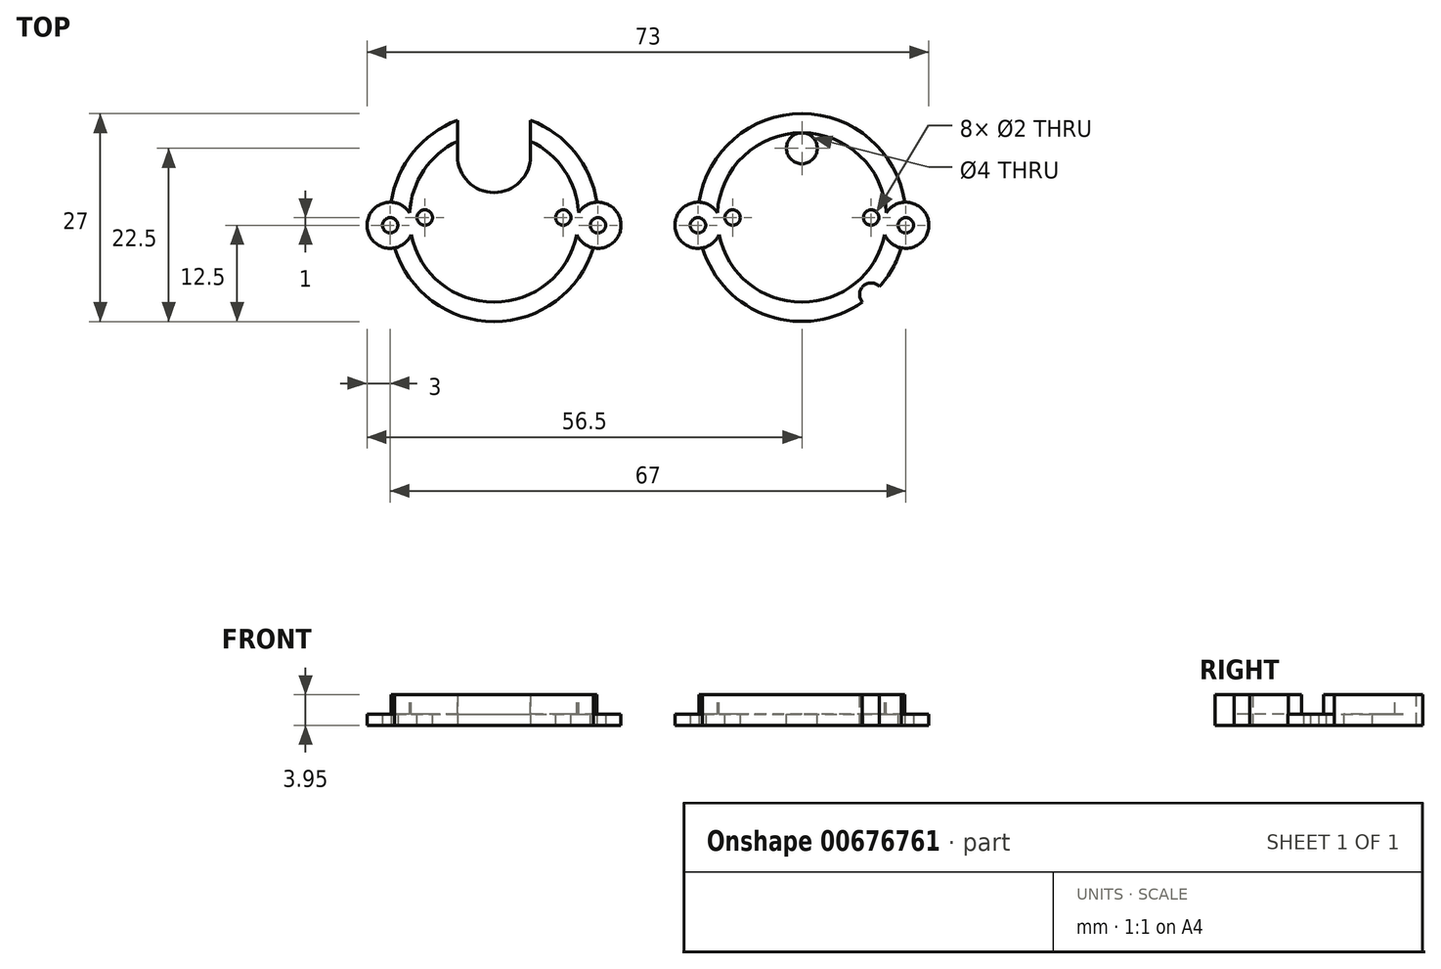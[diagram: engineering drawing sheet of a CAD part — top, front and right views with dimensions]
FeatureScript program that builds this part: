
annotation { "Feature Type Name" : "Feature", "Feature Type Description" : "" }
export const myFeature = defineFeature(function(context is Context, id is Id, definition is map)
    precondition{}
    {
        {
            var Q0;
            Q0=qCreatedBy(makeId("Top.planeOp"),FACE);
            var sketch = newSketch(context, id + "F0", { "sketchPlane" : qUnion([Q0])});
            skArc(sketch, "E0", {"start": v(-12.91, -3.94) * mm, "mid": v(0, -13.5) * mm, "end": v(12.91, -3.94) * mm});
            skCircle(sketch, "E1", {"center": v(-13.5, -1) * mm, "radius": 1 * mm});
            skCircle(sketch, "E2", {"center": v(13.5, -1) * mm, "radius": 1 * mm});
            skArc(sketch, "E3", {"start": v(-12.91, -3.94) * mm, "mid": v(-16.5, -1.22) * mm, "end": v(-13.35, 2) * mm});
            skArc(sketch, "E4", {"start": v(12.91, -3.94) * mm, "mid": v(16.5, -1.22) * mm, "end": v(13.35, 2) * mm});
            skArc(sketch, "E5.trimOffspring", {"start": v(13.35, 2) * mm, "mid": v(0, 13.5) * mm, "end": v(-13.35, 2) * mm});
            skSolve(sketch);
        }
        {
            var Q0;
            Q0=makeQuery(id+"F0.imprint","IMPRINT",FACE,{"disambiguationData":[TD([[makeQuery(id+"F0.imprint","IMPRINT",EDGE,{"derivedFrom":sQuery(id+"F0.wireOp",EDGE,"E0")}),1.0]])]});
            extrude(context, id + "F1", {"entities" : qUnion([Q0]), "depth" : 3.95 * mm, "offsetDistance" : 25 * mm});
        }
        {
            var Q0;
            Q0=makeQuery(id+"F1.opExtrude","CAP_FACE",FACE,{"disambiguationData":[OSD([sQuery(id+"F0.wireOp",EDGE,"E0")])],"isStart":false});
            var sketch = newSketch(context, id + "F2", { "sketchPlane" : qUnion([Q0])});
            skCircle(sketch, "E6", {"center": v(0, 0) * mm, "radius": 11 * mm});
            skSolve(sketch);
        }
        {
            var Q0;
            Q0 = qSketchRegion(id + "F2", true);
            extrude(context, id + "F3", {"entities" : qUnion([Q0]), "operationType" : NewBodyOperationType.REMOVE, "oppositeDirection" : true, "depth" : 2.5 * mm, "offsetDistance" : 25 * mm});
        }
        {
            var Q0;
            Q0=makeQuery(id+"F1.opExtrude","CAP_FACE",FACE,{"disambiguationData":[OSD([sQuery(id+"F0.wireOp",EDGE,"E0"),sQuery(id+"F0.wireOp",EDGE,"E1"),sQuery(id+"F0.wireOp",EDGE,"E2"),sQuery(id+"F0.wireOp",EDGE,"E3"),sQuery(id+"F0.wireOp",EDGE,"E4"),sQuery(id+"F0.wireOp",EDGE,"E5.trimOffspring")])],"isStart":false});
            var sketch = newSketch(context, id + "F4", { "sketchPlane" : qUnion([Q0])});
            skCircle(sketch, "E7", {"center": v(-13.5, -1) * mm, "radius": 3 * mm});
            skCircle(sketch, "E8", {"center": v(13.5, -1) * mm, "radius": 3 * mm});
            skSolve(sketch);
        }
        {
            var Q0;
            Q0 = qSketchRegion(id + "F4", true);
            var Q1;
            Q1=makeQuery(id+"F3.boolean.opBoolean","COPY",FACE,{"derivedFrom":makeQuery(id+"F3.opExtrude","CAP_FACE",FACE,{"disambiguationData":[OSD([sQuery(id+"F2.wireOp",EDGE,"E6")])],"isStart":false})});
            extrude(context, id + "F5", {"entities" : qUnion([Q0]), "operationType" : NewBodyOperationType.REMOVE, "endBound" : BoundingType.UP_TO_SURFACE, "oppositeDirection" : true, "depth" : 25 * mm, "endBoundEntityFace" : qUnion([Q1]), "offsetDistance" : 25 * mm});
        }
        {
            var Q0;
            Q0=makeQuery(id+"F3.boolean.opBoolean","COPY",FACE,{"derivedFrom":makeQuery(id+"F3.opExtrude","CAP_FACE",FACE,{"disambiguationData":[OSD([sQuery(id+"F2.wireOp",EDGE,"E6")])],"isStart":false})});
            var sketch = newSketch(context, id + "F6", { "sketchPlane" : qUnion([Q0])});
            skCircle(sketch, "E9", {"center": v(-9, 0) * mm, "radius": 1 * mm});
            skCircle(sketch, "E10", {"center": v(9, 0) * mm, "radius": 1 * mm});
            skSolve(sketch);
        }
        {
            var Q0;
            Q0=makeQuery(id+"F6.imprint","IMPRINT",FACE,{"disambiguationData":[TD([[makeQuery(id+"F6.imprint","IMPRINT",EDGE,{"derivedFrom":sQuery(id+"F6.wireOp",EDGE,"E9")}),1.0]])]});
            var Q1;
            Q1=makeQuery(id+"F6.imprint","IMPRINT",FACE,{"disambiguationData":[TD([[makeQuery(id+"F6.imprint","IMPRINT",EDGE,{"derivedFrom":sQuery(id+"F6.wireOp",EDGE,"E10")}),1.0]])]});
            extrude(context, id + "F7", {"entities" : qUnion([Q0, Q1]), "operationType" : NewBodyOperationType.REMOVE, "endBound" : BoundingType.THROUGH_ALL, "oppositeDirection" : true, "depth" : 25 * mm, "offsetDistance" : 25 * mm});
        }
        {
            var Q0;
            Q0=makeQuery(id+"F1.opExtrude","SWEPT_BODY",BODY,{"disambiguationData":[OSD([sQuery(id+"F0.wireOp",EDGE,"E0"),sQuery(id+"F0.wireOp",EDGE,"E1"),sQuery(id+"F0.wireOp",EDGE,"E2"),sQuery(id+"F0.wireOp",EDGE,"E3"),sQuery(id+"F0.wireOp",EDGE,"E4"),sQuery(id+"F0.wireOp",EDGE,"E5.trimOffspring")])]});
            transform(context, id + "F8", {"entities" : qUnion([Q0]), "transformType" : TransformType.TRANSLATION_3D, "dx" : 40 * mm, "dy" : 0 * mm, "dz" : 0 * mm, "makeCopy" : true});
        }
        {
            var Q0;
            Q0=makeQuery(id+"F1.opExtrude","CAP_FACE",FACE,{"disambiguationData":[OSD([sQuery(id+"F0.wireOp",EDGE,"E0")])],"isStart":true});
            var sketch = newSketch(context, id + "F9", { "sketchPlane" : qUnion([Q0])});
            skArc(sketch, "E11", {"start": v(4.75, -8) * mm, "mid": v(0, -3.25) * mm, "end": v(-4.75, -8) * mm});
            skLineSegment(sketch, "E12", {"start": v(-4.75, -8) * mm, "end": v(-4.75, -12.64) * mm});
            skLineSegment(sketch, "E13", {"start": v(4.75, -8) * mm, "end": v(4.75, -12.64) * mm});
            skSolve(sketch);
        }
        {
            var Q0;
            Q0=makeQuery(id+"F9.imprint","IMPRINT",FACE,{"disambiguationData":[TD([[makeQuery(id+"F9.imprint","IMPRINT",EDGE,{"derivedFrom":sQuery(id+"F9.wireOp",EDGE,"E11")}),1.0]])]});
            var Q1;
            Q1=makeQuery(id+"F1.opExtrude","CAP_FACE",FACE,{"disambiguationData":[OSD([sQuery(id+"F0.wireOp",EDGE,"E0")])],"isStart":false});
            extrude(context, id + "F10", {"entities" : qUnion([Q0]), "operationType" : NewBodyOperationType.REMOVE, "endBound" : BoundingType.UP_TO_SURFACE, "oppositeDirection" : true, "depth" : 25 * mm, "endBoundEntityFace" : qUnion([Q1]), "offsetDistance" : 25 * mm});
        }
        {
            var Q0;
            {var subQ0=sQuery(id+"F2.wireOp",EDGE,"E6");Q0=makeQuery(id+"F8.opPattern","COPY",FACE,{"derivedFrom":makeQuery(id+"F5.boolean.opBoolean","MERGE",FACE,{"derivedFrom":[makeQuery(id+"F3.boolean.opBoolean","COPY",FACE,{"derivedFrom":makeQuery(id+"F3.opExtrude","CAP_FACE",FACE,{"disambiguationData":[OSD([subQ0])],"isStart":false})}),makeQuery(id+"F5.opExtrude","CAP_FACE",FACE,{"disambiguationData":[OSD([subQ0]),OD(0.0)],"isStart":false}),makeQuery(id+"F5.opExtrude","CAP_FACE",FACE,{"disambiguationData":[OSD([subQ0]),OD(1.0)],"isStart":false})]}),"instanceName":"1"});}
            var sketch = newSketch(context, id + "F11", { "sketchPlane" : qUnion([Q0])});
            skCircle(sketch, "E14", {"center": v(40, 9) * mm, "radius": 2 * mm});
            skCircle(sketch, "E15", {"center": v(49, -10) * mm, "radius": 1.5 * mm});
            skPoint(sketch, "E16", {"position": v(26.5, -1) * mm});
            skSolve(sketch);
        }
        {
            var Q0;
            Q0=makeQuery(id+"F11.imprint","IMPRINT",FACE,{"disambiguationData":[TD([[makeQuery(id+"F11.imprint","IMPRINT",EDGE,{"derivedFrom":sQuery(id+"F11.wireOp",EDGE,"E15")}),1.0]])]});
            var Q1;
            Q1=makeQuery(id+"F11.imprint","IMPRINT",FACE,{"disambiguationData":[TD([[makeQuery(id+"F11.imprint","IMPRINT",EDGE,{"derivedFrom":sQuery(id+"F11.wireOp",EDGE,"E14")}),1.0]])]});
            var Q2;
            {var subQ0=sQuery(id+"F0.wireOp",EDGE,"E0");Q2=makeQuery(id+"F8.opPattern","COPY",FACE,{"derivedFrom":makeQuery(id+"F5.boolean.opBoolean","SPLIT",FACE,{"disambiguationData":[TD([makeQuery(id+"F1.opExtrude","SWEPT_FACE",FACE,{"disambiguationData":[OSD([subQ0])]})])],"derivedFrom":makeQuery(id+"F1.opExtrude","CAP_FACE",FACE,{"disambiguationData":[OSD([subQ0,sQuery(id+"F0.wireOp",EDGE,"E1"),sQuery(id+"F0.wireOp",EDGE,"E2"),sQuery(id+"F0.wireOp",EDGE,"E3"),sQuery(id+"F0.wireOp",EDGE,"E4"),sQuery(id+"F0.wireOp",EDGE,"E5.trimOffspring")])],"isStart":false})}),"instanceName":"1"});}
            extrude(context, id + "F12", {"entities" : qUnion([Q0, Q1]), "operationType" : NewBodyOperationType.REMOVE, "endBound" : BoundingType.UP_TO_NEXT, "oppositeDirection" : true, "depth" : 25 * mm, "offsetDistance" : 25 * mm, "hasSecondDirection" : true, "secondDirectionBound" : SecondDirectionBoundingType.UP_TO_SURFACE, "secondDirectionOppositeDirection" : false, "secondDirectionDepth" : 25 * mm, "secondDirectionBoundEntityFace" : qUnion([Q2])});
        }
    });
